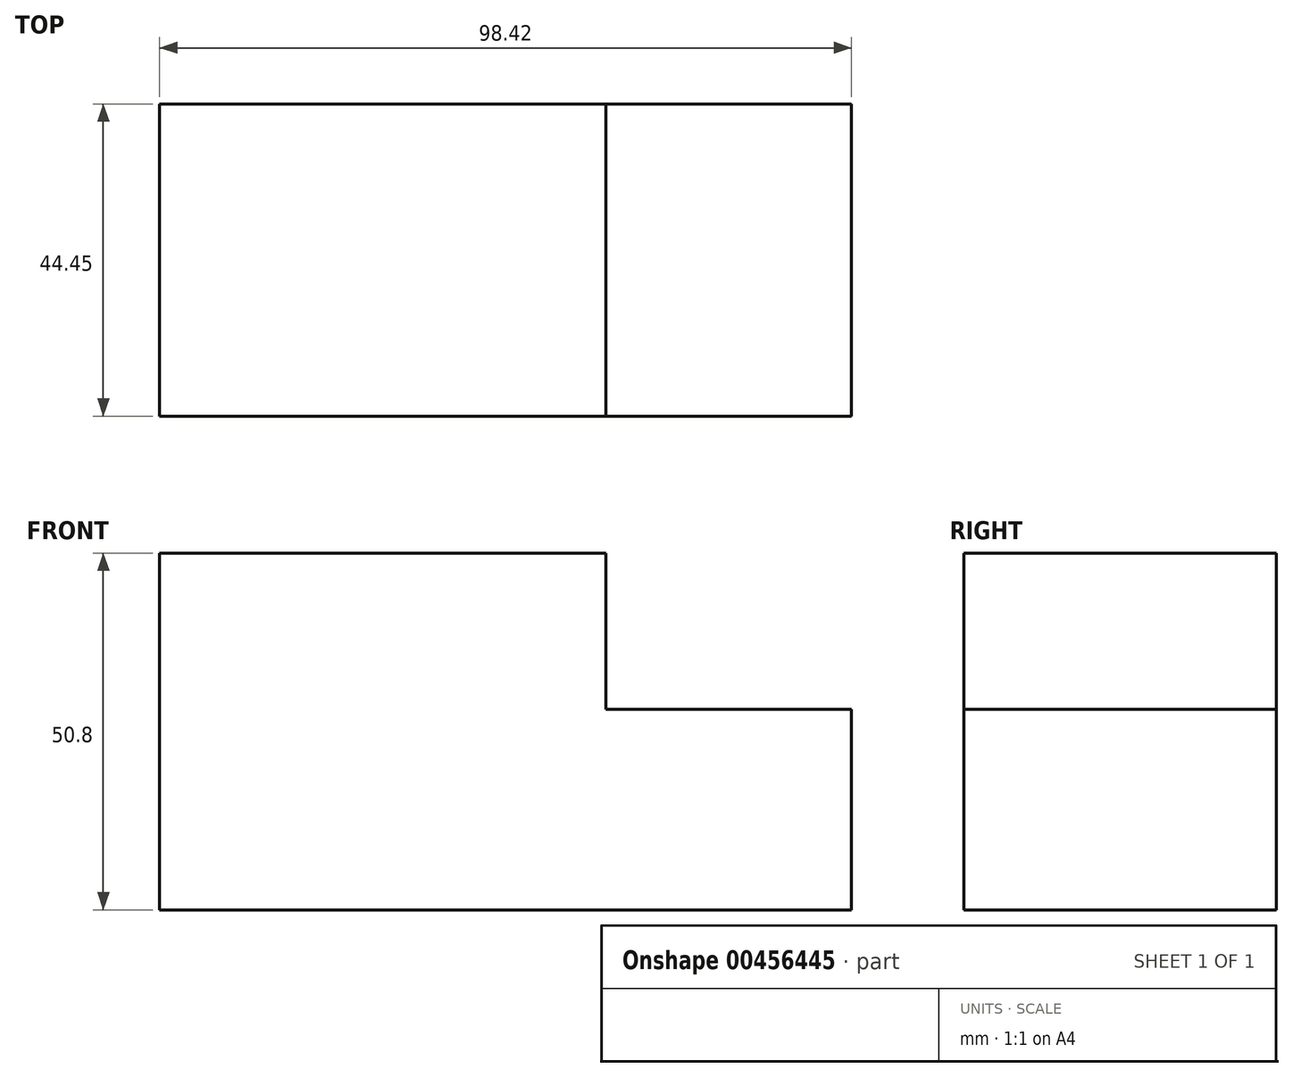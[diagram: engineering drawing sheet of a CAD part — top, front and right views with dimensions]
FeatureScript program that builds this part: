
annotation { "Feature Type Name" : "Feature", "Feature Type Description" : "" }
export const myFeature = defineFeature(function(context is Context, id is Id, definition is map)
    precondition{}
    {
        {
            var Q0;
            Q0=qCreatedBy(makeId("Front.planeOp"),FACE);
            var sketch = newSketch(context, id + "F0", { "sketchPlane" : qUnion([Q0])});
            skLineSegment(sketch, "E0.bottom", {"start": v(49.21, -14.29) * mm, "end": v(-49.21, -14.29) * mm});
            skLineSegment(sketch, "E0.top", {"start": v(49.21, 14.29) * mm, "end": v(14.29, 14.29) * mm});
            skLineSegment(sketch, "E0.left", {"start": v(49.21, -14.29) * mm, "end": v(49.21, 14.29) * mm});
            skLineSegment(sketch, "E0.right", {"start": v(-49.21, -14.29) * mm, "end": v(-49.21, 14.29) * mm});
            skPoint(sketch, "E0.middle", {"position": v(0, 0) * mm});
            skLineSegment(sketch, "E1.top", {"start": v(-49.21, 36.51) * mm, "end": v(14.29, 36.51) * mm});
            skLineSegment(sketch, "E1.left", {"start": v(-49.21, 14.29) * mm, "end": v(-49.21, 36.51) * mm});
            skLineSegment(sketch, "E1.right", {"start": v(14.29, 14.29) * mm, "end": v(14.29, 36.51) * mm});
            skSolve(sketch);
        }
        {
            var Q0;
            Q0=makeQuery(id+"F0.imprint","IMPRINT",FACE,{"disambiguationData":[TD([[makeQuery(id+"F0.imprint","IMPRINT",EDGE,{"derivedFrom":sQuery(id+"F0.wireOp",EDGE,"E0.bottom")}),-1.0]])]});
            extrude(context, id + "F1", {"entities" : qUnion([Q0]), "depth" : 44.45 * mm});
        }
    });
